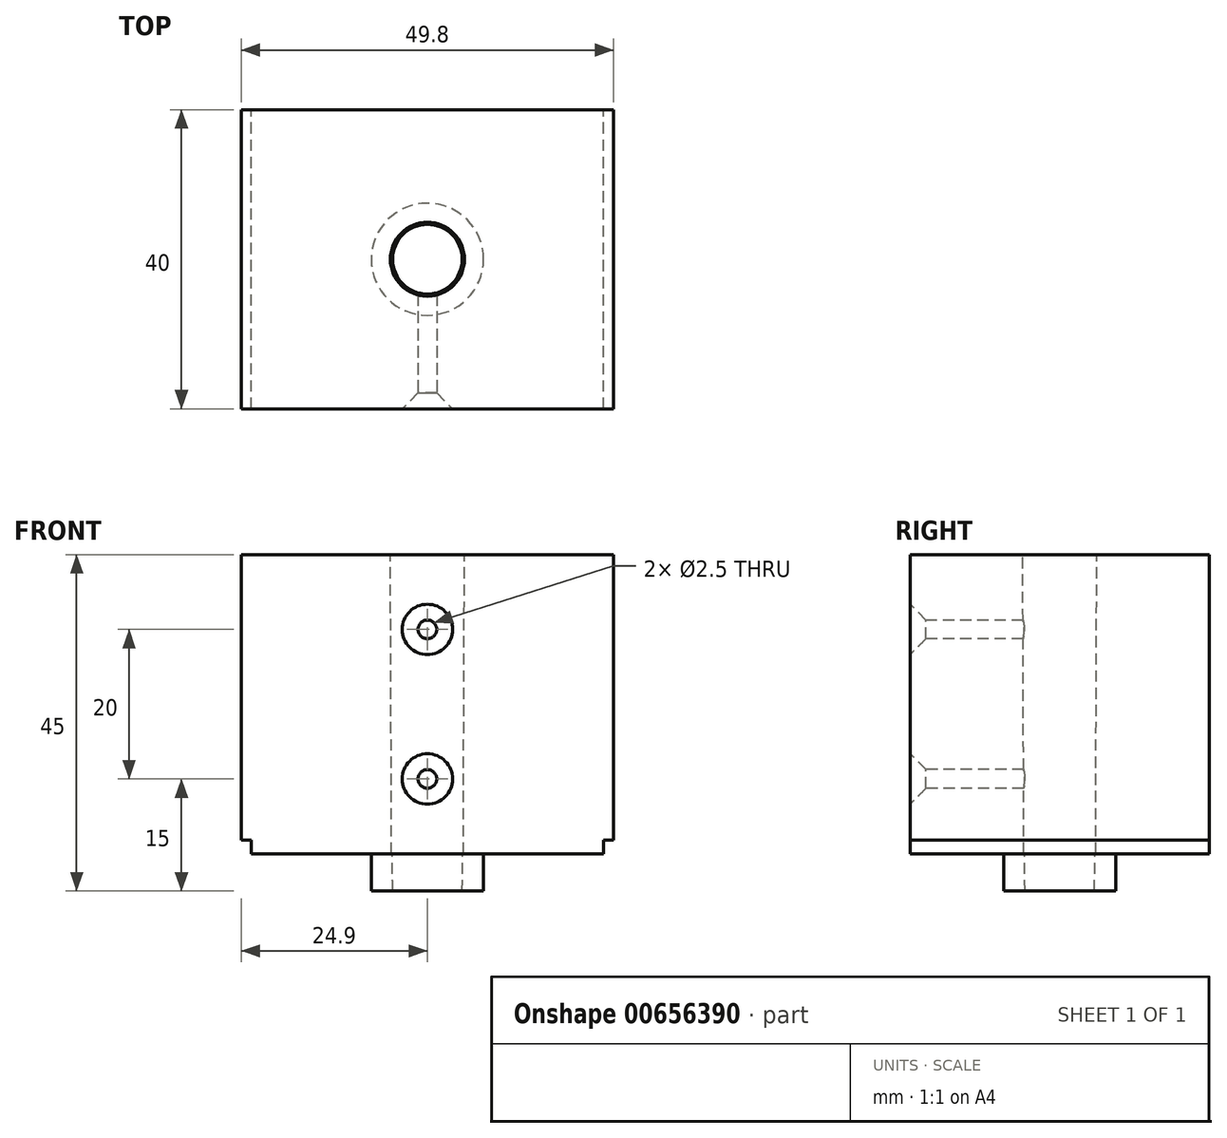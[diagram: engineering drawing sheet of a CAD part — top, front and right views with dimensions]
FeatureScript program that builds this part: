
annotation { "Feature Type Name" : "Feature", "Feature Type Description" : "" }
export const myFeature = defineFeature(function(context is Context, id is Id, definition is map)
    precondition{}
    {
        {
            var Q0;
            Q0=qCreatedBy(makeId("Front.planeOp"),FACE);
            var sketch = newSketch(context, id + "F0", { "sketchPlane" : qUnion([Q0])});
            skLineSegment(sketch, "E0.bottom", {"start": v(-24.9, 40) * mm, "end": v(24.9, 40) * mm});
            skLineSegment(sketch, "E0.top", {"start": v(-24.9, 0) * mm, "end": v(24.9, 0) * mm});
            skLineSegment(sketch, "E0.left", {"start": v(-24.9, 40) * mm, "end": v(-24.9, 0) * mm});
            skLineSegment(sketch, "E0.right", {"start": v(24.9, 40) * mm, "end": v(24.9, 0) * mm});
            skLineSegment(sketch, "E1.bottom", {"start": v(24.9, 0) * mm, "end": v(23.57, 0) * mm});
            skLineSegment(sketch, "E1.top", {"start": v(24.9, 1.85) * mm, "end": v(23.57, 1.85) * mm});
            skLineSegment(sketch, "E1.left", {"start": v(24.9, 0) * mm, "end": v(24.9, 1.85) * mm});
            skLineSegment(sketch, "E1.right", {"start": v(23.57, 0) * mm, "end": v(23.57, 1.85) * mm});
            skLineSegment(sketch, "E2.bottom", {"start": v(-24.9, 0) * mm, "end": v(-23.58, 0) * mm});
            skLineSegment(sketch, "E2.top", {"start": v(-24.9, 1.85) * mm, "end": v(-23.58, 1.85) * mm});
            skLineSegment(sketch, "E2.left", {"start": v(-24.9, 0) * mm, "end": v(-24.9, 1.85) * mm});
            skLineSegment(sketch, "E2.right", {"start": v(-23.58, 0) * mm, "end": v(-23.58, 1.85) * mm});
            skSolve(sketch);
        }
        {
            var Q0;
            Q0=makeQuery(id+"F0.imprint","IMPRINT",FACE,{"disambiguationData":[TD([[makeQuery(id+"F0.imprint","IMPRINT",EDGE,{"derivedFrom":sQuery(id+"F0.wireOp",EDGE,"E0.bottom")}),-1.0]])]});
            extrude(context, id + "F1", {"entities" : qUnion([Q0]), "depth" : 40 * mm, "offsetDistance" : 25 * mm});
        }
        {
            var Q0;
            Q0=makeQuery(id+"F1.opExtrude","SWEPT_FACE",FACE,{"disambiguationData":[OSD([sQuery(id+"F0.wireOp",EDGE,"E0.top")])]});
            var sketch = newSketch(context, id + "F2", { "sketchPlane" : qUnion([Q0])});
            skPoint(sketch, "E3", {"position": v(0, 20) * mm});
            skPoint(sketch, "E3.positionSnap0", {"position": v(23.57, 20) * mm});
            skCircle(sketch, "E4", {"center": v(0, 20) * mm, "radius": 7.5 * mm});
            skSolve(sketch);
        }
        {
            var Q0;
            Q0=makeQuery(id+"F2.imprint","IMPRINT",FACE,{"disambiguationData":[TD([[makeQuery(id+"F2.imprint","IMPRINT",EDGE,{"derivedFrom":sQuery(id+"F2.wireOp",EDGE,"E4")}),1.0]])]});
            extrude(context, id + "F3", {"entities" : qUnion([Q0]), "operationType" : NewBodyOperationType.ADD, "depth" : 5 * mm, "offsetDistance" : 25 * mm});
        }
        {
            var Q0;
            Q0=makeQuery(id+"F1.opExtrude","SWEPT_FACE",FACE,{"disambiguationData":[OSD([sQuery(id+"F0.wireOp",EDGE,"E0.bottom")])]});
            var sketch = newSketch(context, id + "F4", { "sketchPlane" : qUnion([Q0])});
            skLineSegment(sketch, "E5", {"start": v(-24.9, -20) * mm, "end": v(24.9, -20) * mm, "construction": true});
            skSolve(sketch);
        }
        {
            var Q0;
            Q0=sQuery(id+"F4.wireOp",EDGE,"E5");
            cPlane(context, id + "F5", {"entities" : qUnion([Q0]), "cplaneType" : CPlaneType.LINE_ANGLE, "offset" : 25 * mm, "angle" : 0 * degree, "width" : 150 * mm, "height" : 150 * mm});
        }
        {
            var Q0;
            Q0=qCreatedBy(id+"F5.planeOp",FACE);
            var sketch = newSketch(context, id + "F6", { "sketchPlane" : qUnion([Q0])});
            skLineSegment(sketch, "E6", {"start": v(0, 0) * mm, "end": v(0, 60.96) * mm, "construction": true});
            skLineSegment(sketch, "E7", {"start": v(4.95, 40) * mm, "end": v(4.8, 0) * mm});
            skLineSegment(sketch, "E8", {"start": v(0, 0) * mm, "end": v(0, -12.99) * mm, "construction": true});
            skLineSegment(sketch, "E9", {"start": v(4.72, 0) * mm, "end": v(4.65, -5) * mm});
            skLineSegment(sketch, "E10", {"start": v(4.8, 0) * mm, "end": v(4.72, 0) * mm});
            skLineSegment(sketch, "E11", {"start": v(4.95, 40) * mm, "end": v(0, 40) * mm});
            skLineSegment(sketch, "E12", {"start": v(4.65, -5) * mm, "end": v(0, -5) * mm});
            skLineSegment(sketch, "E13", {"start": v(0, 0) * mm, "end": v(0, 40) * mm});
            skLineSegment(sketch, "E14", {"start": v(0, -5) * mm, "end": v(0, 0) * mm});
            skSolve(sketch);
        }
        {
            var Q0;
            Q0=makeQuery(id+"F6.imprint","IMPRINT",FACE,{"disambiguationData":[TD([[makeQuery(id+"F6.imprint","IMPRINT",EDGE,{"derivedFrom":sQuery(id+"F6.wireOp",EDGE,"E7")}),-1.0]])]});
            var Q1;
            Q1=sQuery(id+"F6.wireOp",EDGE,"E6");
            revolve(context, id + "F7", {"entities" : qUnion([Q0]), "axis" : qUnion([Q1]), "revolveType" : RevolveType.FULL});
        }
        {
            var Q0;
            Q0=makeQuery(id+"F7.opRevolve","SWEPT_BODY",BODY,{"disambiguationData":[OSD([sQuery(id+"F6.wireOp",EDGE,"E7"),sQuery(id+"F6.wireOp",EDGE,"E9"),sQuery(id+"F6.wireOp",EDGE,"E10"),sQuery(id+"F6.wireOp",EDGE,"E11"),sQuery(id+"F6.wireOp",EDGE,"E12"),sQuery(id+"F6.wireOp",EDGE,"E13"),sQuery(id+"F6.wireOp",EDGE,"E14")])]});
            var Q1;
            Q1=makeQuery(id+"F1.opExtrude","SWEPT_BODY",BODY,{"disambiguationData":[OSD([sQuery(id+"F0.wireOp",EDGE,"E0.bottom"),sQuery(id+"F0.wireOp",EDGE,"E0.top"),sQuery(id+"F0.wireOp",EDGE,"E0.left"),sQuery(id+"F0.wireOp",EDGE,"E0.right"),sQuery(id+"F0.wireOp",EDGE,"E1.top"),sQuery(id+"F0.wireOp",EDGE,"E1.right"),sQuery(id+"F0.wireOp",EDGE,"E2.top"),sQuery(id+"F0.wireOp",EDGE,"E2.right")])]});
            booleanBodies(context, id + "F8", {"operationType" : BooleanOperationType.SUBTRACTION, "tools" : qUnion([Q0]), "targets" : qUnion([Q1])});
        }
        {
            var Q0;
            Q0=makeQuery(id+"F1.opExtrude","CAP_FACE",FACE,{"disambiguationData":[OSD([sQuery(id+"F0.wireOp",EDGE,"E0.bottom"),sQuery(id+"F0.wireOp",EDGE,"E0.top"),sQuery(id+"F0.wireOp",EDGE,"E0.left"),sQuery(id+"F0.wireOp",EDGE,"E0.right"),sQuery(id+"F0.wireOp",EDGE,"E1.top"),sQuery(id+"F0.wireOp",EDGE,"E1.right"),sQuery(id+"F0.wireOp",EDGE,"E2.top"),sQuery(id+"F0.wireOp",EDGE,"E2.right")])],"isStart":false});
            var sketch = newSketch(context, id + "F9", { "sketchPlane" : qUnion([Q0])});
            skPoint(sketch, "E15", {"position": v(0, 30) * mm});
            skPoint(sketch, "E16", {"position": v(0, 10) * mm});
            skSolve(sketch);
        }
        {
            var Q0;
            Q0=sQuery(id+"F9.wireOp",VERTEX,"E15");
            var Q1;
            Q1=sQuery(id+"F9.wireOp",VERTEX,"E16");
            var Q2;
            Q2=makeQuery(id+"F1.opExtrude","SWEPT_BODY",BODY,{"disambiguationData":[OSD([sQuery(id+"F0.wireOp",EDGE,"E0.bottom"),sQuery(id+"F0.wireOp",EDGE,"E0.top"),sQuery(id+"F0.wireOp",EDGE,"E0.left"),sQuery(id+"F0.wireOp",EDGE,"E0.right"),sQuery(id+"F0.wireOp",EDGE,"E1.top"),sQuery(id+"F0.wireOp",EDGE,"E1.right"),sQuery(id+"F0.wireOp",EDGE,"E2.top"),sQuery(id+"F0.wireOp",EDGE,"E2.right")])]});
            hole(context, id + "F10", {"style" : HoleStyle.C_SINK, "endStyle" : HoleEndStyle.BLIND, "standardTappedOrClearance" : lookupTablePath({ "standard" : "ISO", "engagement" : "75%", "pitch" : "0.5 mm", "size" : "M3", "type" : "Tapped" }), "standardBlindInLast" : lookupTablePath({ "standard" : "ISO", "engagement" : "75%", "pitch" : "0.5 mm", "size" : "M3", "type" : "Tapped" }), "holeDiameter" : 2.5 * mm, "cSinkDiameter" : 6.72 * mm, "cSinkAngle" : 90 * degree, "majorDiameter" : 3 * mm, "showTappedDepth" : true, "holeDepth" : 16 * mm, "isTappedThrough" : true, "tappedDepth" : 14.5 * mm, "tapClearance" : 3, "startFromSketch" : true, "locations" : qUnion([Q0, Q1]), "scope" : qUnion([Q2])});
        }
    });
